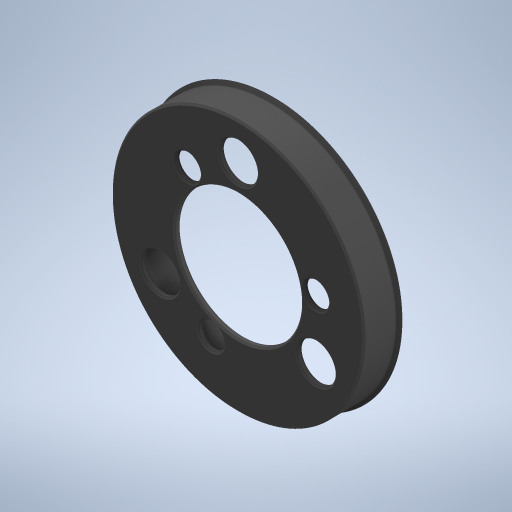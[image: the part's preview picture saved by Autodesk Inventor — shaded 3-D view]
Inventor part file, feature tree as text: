
AUTODESK INVENTOR PART (.ipt)
format: ipt  version: 2023 (Build 270158000, 158)  size: 353,792 bytes
history: native  units: mm
features: chamfer x4, extrude x3, sketch x3
ambient origin geometry x8: Origin, YZ Plane, XZ Plane, XY Plane, X Axis, Y Axis, Z Axis, Center Point
bodies: Solid1 (feature_tree)
feature tree (10):
  extrude  "Extrusion1"  Depth=69.85mm
  extrude  "Extrusion2"  Depth=9.6mm
  extrude  "Extrusion3"  Depth=50.0mm
  chamfer  "Chamfer1"  Distance=12.0mm
  chamfer  "Chamfer2"  Distance=6.981317mm
  chamfer  "Chamfer3"  Distance=8.0mm
  chamfer  "Chamfer4"  Distance=30.0mm Angle=360.0deg
  sketch  "Sketch1"  dims[d0=80.1mm d1=69.85mm]
  sketch  "Sketch2"  dims[d2=9.6mm d3=0.0mm d4=40.0mm]
  sketch  "Sketch3"  dims[d5=57.0mm d6=50.0mm d7=12.0mm d8=6.981317mm d9=8.0mm d10=30.0mm d12=360.0deg d14=2.0mm d15=0.0mm d16=1.0mm d17=1.0mm d18=0.0mm d19=0.5mm d20=2.0mm d21=45.0deg d22=1.0mm d23=2.0mm d24=45.0deg d25=0.5mm d26=2.0mm d27=45.0deg d28=0.5mm d29=2.0mm d30=45.0deg]
